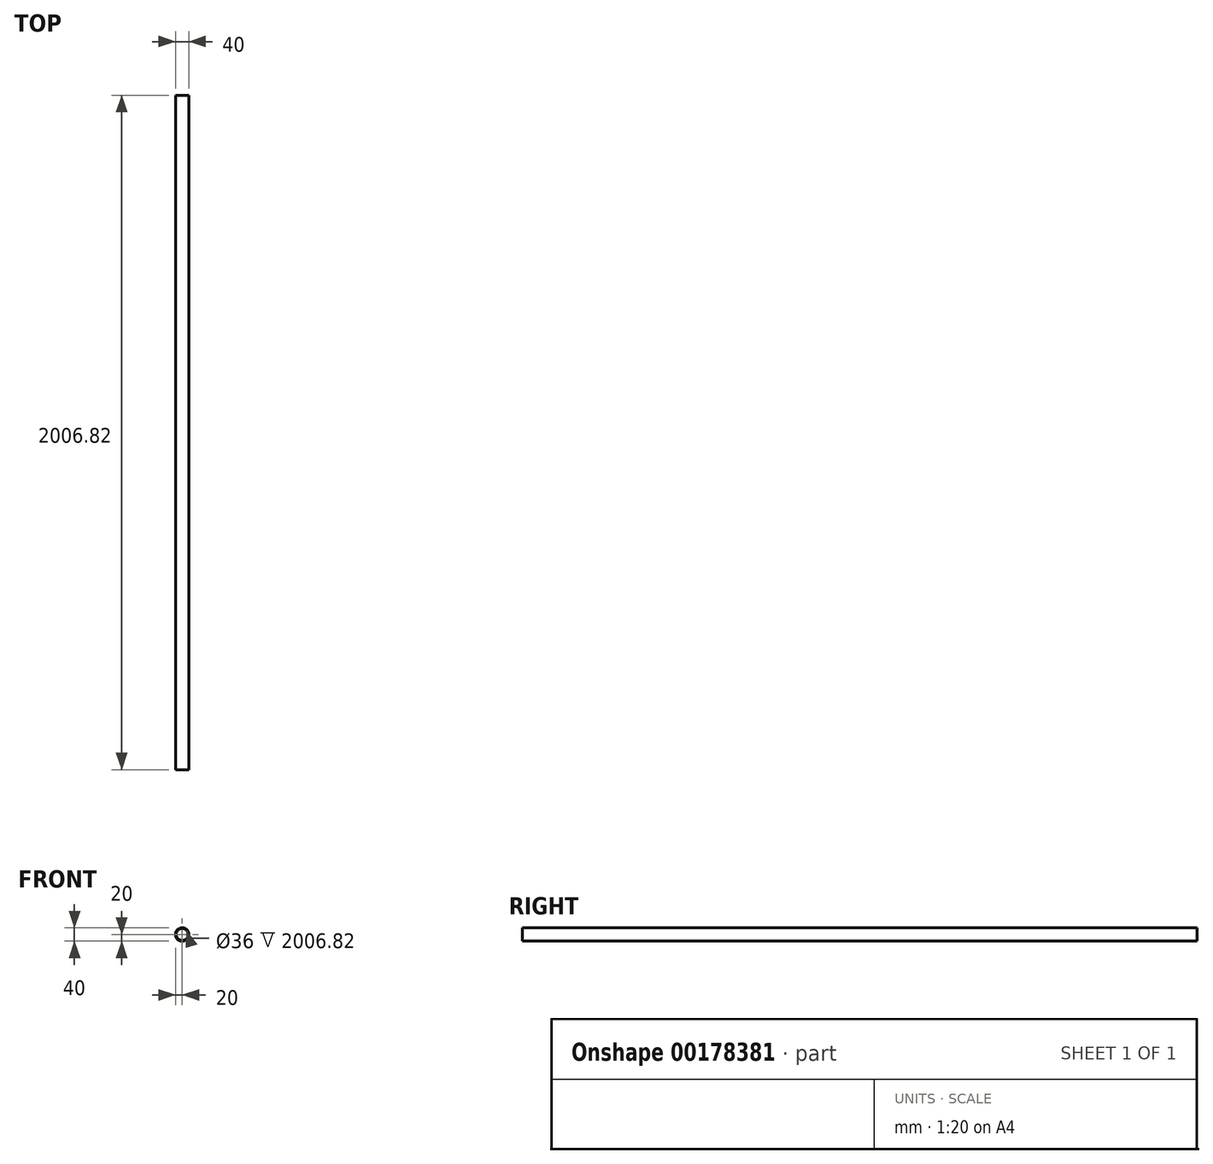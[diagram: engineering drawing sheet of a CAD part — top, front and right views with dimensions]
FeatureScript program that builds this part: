
annotation { "Feature Type Name" : "Feature", "Feature Type Description" : "" }
export const myFeature = defineFeature(function(context is Context, id is Id, definition is map)
    precondition{}
    {
        {
            var Q0;
            Q0=qCreatedBy(makeId("Front.planeOp"),FACE);
            var sketch = newSketch(context, id + "F0", { "sketchPlane" : qUnion([Q0])});
            skCircle(sketch, "E0", {"center": v(0, 0) * mm, "radius": 20 * mm});
            skCircle(sketch, "E1.0", {"center": v(0, 0) * mm, "radius": 18 * mm});
            skSolve(sketch);
        }
        {
            var Q0;
            Q0=makeQuery(id+"F0.imprint","IMPRINT",FACE,{"disambiguationData":[TD([[makeQuery(id+"F0.imprint","IMPRINT",EDGE,{"derivedFrom":sQuery(id+"F0.wireOp",EDGE,"E0")}),1.0]])]});
            extrude(context, id + "F1", {"entities" : qUnion([Q0]), "depth" : 2006.82 * mm});
        }
    });
